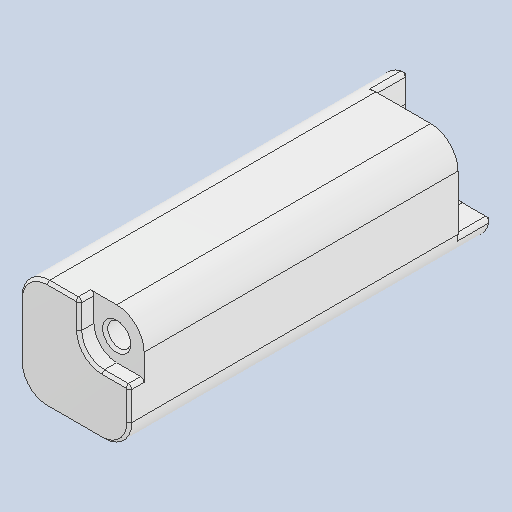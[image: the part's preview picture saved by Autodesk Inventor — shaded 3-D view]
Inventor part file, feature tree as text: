
AUTODESK INVENTOR PART (.ipt)
format: ipt  version: 2023.3 (Build 273359000, 359)  size: 183,296 bytes
history: native  units: mm
features: fillet x4, sketch x4, extrude x3, hole x1, chamfer x1
ambient origin geometry x8: Origin, YZ Plane, XZ Plane, XY Plane, X Axis, Y Axis, Z Axis, Center Point
bodies: Solid1 (feature_tree)
feature tree (13):
  extrude  "Extrusion1"  Depth=25.4mm
  extrude  "Extrusion2"  Depth=11.621mm
  extrude  "Extrusion3"  Depth=3.429mm TaperAngle=0.0deg
  hole  "Hole1"  [1 undecoded]
  fillet  "Fillet1"  Radius=7.938mm
  fillet  "Fillet2"  Radius=6.35mm
  fillet  "Fillet3"  Radius=6.35mm
  fillet  "Fillet4"  Radius=6.35mm
  chamfer  "Chamfer1"  Distance=0.794mm
  sketch  "Sketch1"  dims[d0=25.4mm d1=25.4mm]
  sketch  "Sketch2"  dims[d2=84.138mm d3=0.0mm d4=11.621mm]
  sketch  "Sketch3"  dims[d5=11.621mm d6=3.429mm d7=0.0mm]
  sketch  "Sketch4"  dims[d8=19.558mm d9=19.558mm d10=7.938mm d11=0.0mm d12=6.35mm d13=6.35mm d14=5.334mm d15=6.0mm d16=9.779mm d17=2.0mm d18=14.3117mm d19=8.0mm d20=20.594885mm d21=6.35mm d22=0.794mm d23=5.271mm d24=13.208mm d25=0.6mm d26=2.0mm d27=45.0deg]
note: 1 required parameter value undecoded (feature->parameter linkage not recoverable at this tier; creation-order binding heuristic only, values carry confidence <= 0.55)
